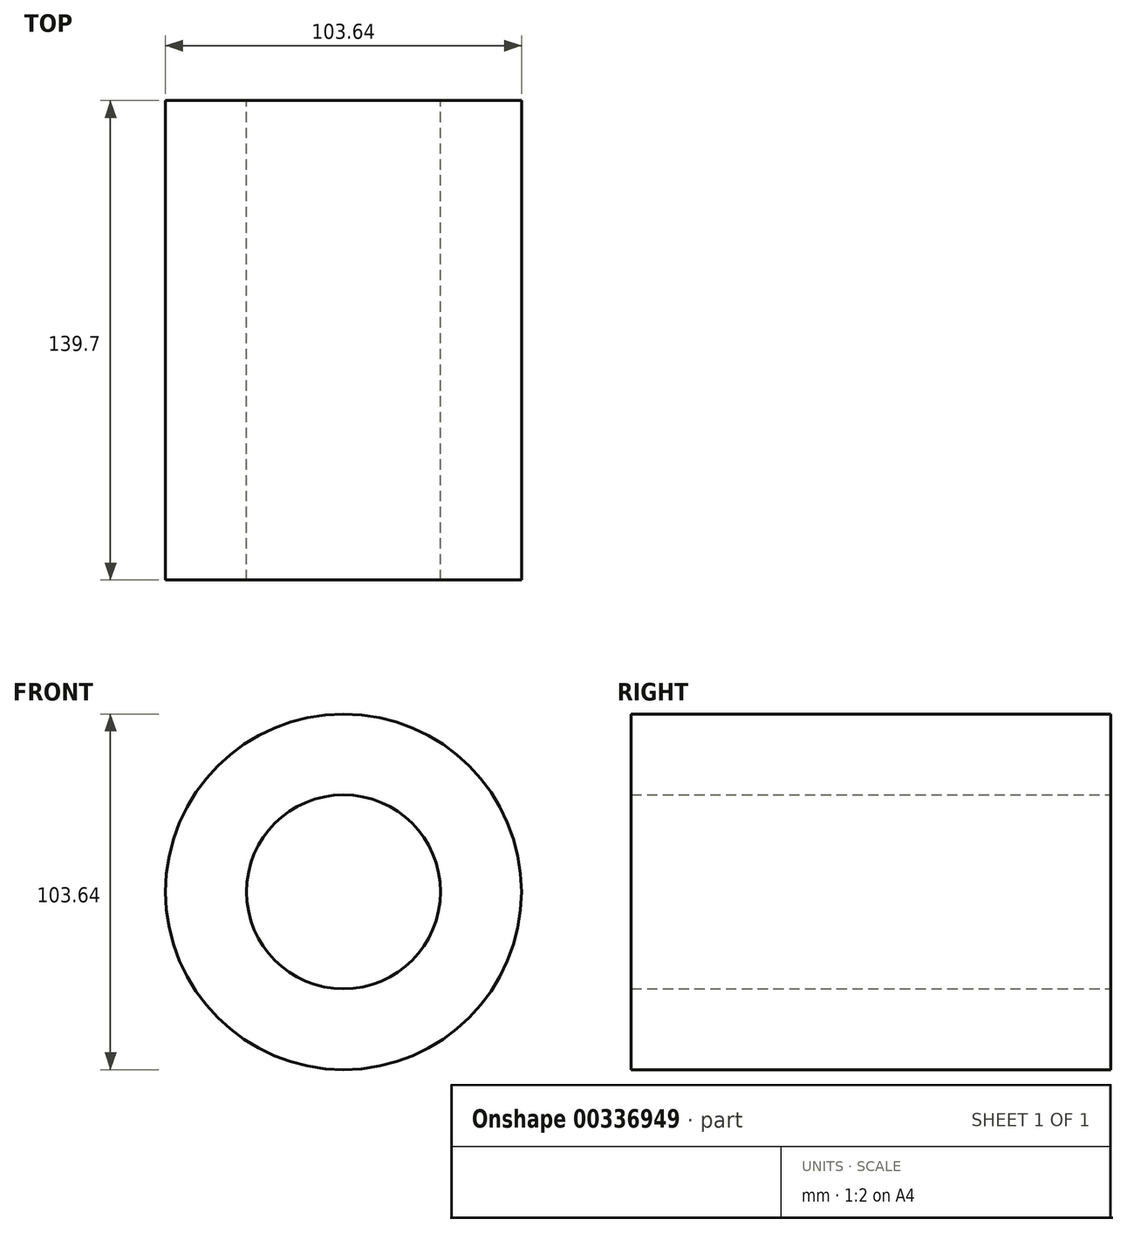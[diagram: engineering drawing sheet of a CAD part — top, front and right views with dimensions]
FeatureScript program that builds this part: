
annotation { "Feature Type Name" : "Feature", "Feature Type Description" : "" }
export const myFeature = defineFeature(function(context is Context, id is Id, definition is map)
    precondition{}
    {
        {
            var Q0;
            Q0=qCreatedBy(makeId("Front.planeOp"),FACE);
            var sketch = newSketch(context, id + "F0", { "sketchPlane" : qUnion([Q0])});
            skCircle(sketch, "E0", {"center": v(0, 0) * mm, "radius": 51.82 * mm});
            skCircle(sketch, "E1", {"center": v(0, 0) * mm, "radius": 28.26 * mm});
            skLineSegment(sketch, "E2.bottom", {"start": v(-55.28, -60.44) * mm, "end": v(-3.7, -60.44) * mm});
            skLineSegment(sketch, "E2.top", {"start": v(-80.8, -16.87) * mm, "end": v(-29.23, -16.87) * mm});
            skLineSegment(sketch, "E2.right", {"start": v(-3.7, -60.44) * mm, "end": v(-29.23, -16.87) * mm});
            skSolve(sketch);
        }
        {
            var Q0;
            Q0 = qSketchRegion(id + "F0", true);
            extrude(context, id + "F1", {"entities" : qUnion([Q0]), "depth" : 139.7 * mm});
        }
    });
